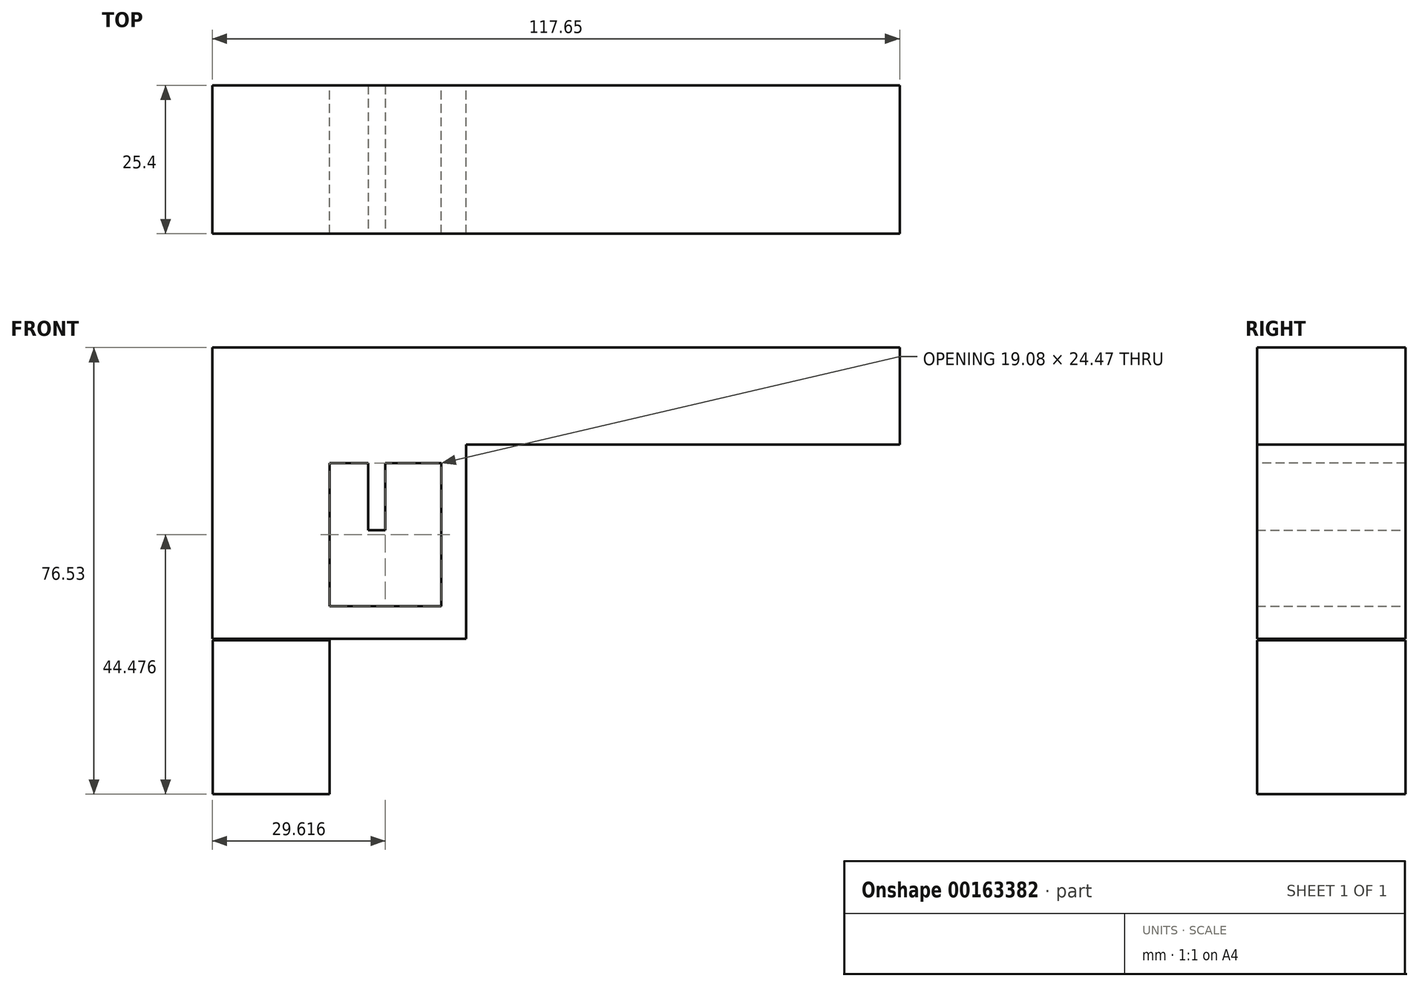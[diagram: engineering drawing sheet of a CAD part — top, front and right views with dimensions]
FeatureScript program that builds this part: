
annotation { "Feature Type Name" : "Feature", "Feature Type Description" : "" }
export const myFeature = defineFeature(function(context is Context, id is Id, definition is map)
    precondition{}
    {
        {
            var Q0;
            Q0=qCreatedBy(makeId("Front.planeOp"),FACE);
            var sketch = newSketch(context, id + "F0", { "sketchPlane" : qUnion([Q0])});
            skLineSegment(sketch, "E0.bottom", {"start": v(-43.44, 19.82) * mm, "end": v(75.73, 19.82) * mm});
            skLineSegment(sketch, "E0.top", {"start": v(-43.44, -30.1) * mm, "end": v(75.73, -30.1) * mm});
            skLineSegment(sketch, "E0.left", {"start": v(-43.44, 19.82) * mm, "end": v(-43.44, -30.1) * mm});
            skLineSegment(sketch, "E0.right", {"start": v(75.73, 19.82) * mm, "end": v(75.73, -30.1) * mm});
            skLineSegment(sketch, "E1.bottom", {"start": v(-35.12, -49.18) * mm, "end": v(-35.85, -49.18) * mm});
            skLineSegment(sketch, "E1.top", {"start": v(-35.12, -48.94) * mm, "end": v(-35.85, -48.94) * mm});
            skLineSegment(sketch, "E1.left", {"start": v(-35.12, -49.18) * mm, "end": v(-35.12, -48.94) * mm});
            skLineSegment(sketch, "E1.right", {"start": v(-35.85, -49.18) * mm, "end": v(-35.85, -48.94) * mm});
            skSolve(sketch);
        }
        {
            var Q0;
            Q0=qCreatedBy(makeId("Front.planeOp"),FACE);
            var sketch = newSketch(context, id + "F1", { "sketchPlane" : qUnion([Q0])});
            skLineSegment(sketch, "E2.bottom", {"start": v(0, -30.1) * mm, "end": v(75.49, -30.1) * mm});
            skLineSegment(sketch, "E2.top", {"start": v(0, 3.18) * mm, "end": v(75.49, 3.18) * mm});
            skLineSegment(sketch, "E2.left", {"start": v(0, -30.1) * mm, "end": v(0, 3.18) * mm});
            skLineSegment(sketch, "E2.right", {"start": v(75.49, -30.1) * mm, "end": v(75.49, 3.18) * mm});
            skSolve(sketch);
        }
        {
            var Q0;
            Q0 = qSketchRegion(id + "F0", true);
            extrude(context, id + "F2", {"entities" : qUnion([Q0]), "depth" : 25.4 * mm});
        }
        {
            var Q0;
            Q0 = qSketchRegion(id + "F1", true);
            extrude(context, id + "F3", {"entities" : qUnion([Q0]), "operationType" : NewBodyOperationType.REMOVE, "depth" : 25.65 * mm});
        }
        {
            var Q0;
            Q0=makeQuery(id+"F2.opExtrude","SWEPT_FACE",FACE,{"disambiguationData":[OSD([sQuery(id+"F0.wireOp",EDGE,"E0.right")])]});
            extrude(context, id + "F4", {"entities" : qUnion([Q0]), "operationType" : NewBodyOperationType.REMOVE, "oppositeDirection" : true, "depth" : 1.52 * mm});
        }
        {
            var Q0;
            Q0=qCreatedBy(makeId("Front.planeOp"),FACE);
            var sketch = newSketch(context, id + "F5", { "sketchPlane" : qUnion([Q0])});
            skLineSegment(sketch, "E3.bottom", {"start": v(-4.28, 0) * mm, "end": v(-23.37, 0) * mm});
            skLineSegment(sketch, "E3.top", {"start": v(-4.28, -24.47) * mm, "end": v(-23.37, -24.47) * mm});
            skLineSegment(sketch, "E3.left", {"start": v(-4.28, 0) * mm, "end": v(-4.28, -24.47) * mm});
            skLineSegment(sketch, "E3.right", {"start": v(-23.37, 0) * mm, "end": v(-23.37, -24.47) * mm});
            skSolve(sketch);
        }
        {
            var Q0;
            Q0 = qSketchRegion(id + "F5", true);
            extrude(context, id + "F6", {"entities" : qUnion([Q0]), "operationType" : NewBodyOperationType.REMOVE, "depth" : 52.32 * mm});
        }
        {
            var Q0;
            Q0=qCreatedBy(makeId("Front.planeOp"),FACE);
            var sketch = newSketch(context, id + "F7", { "sketchPlane" : qUnion([Q0])});
            skLineSegment(sketch, "E4.bottom", {"start": v(-23.37, -30.35) * mm, "end": v(-43.36, -30.35) * mm});
            skLineSegment(sketch, "E4.top", {"start": v(-23.37, -56.71) * mm, "end": v(-43.36, -56.71) * mm});
            skLineSegment(sketch, "E4.left", {"start": v(-23.37, -30.35) * mm, "end": v(-23.37, -56.71) * mm});
            skLineSegment(sketch, "E4.right", {"start": v(-43.36, -30.35) * mm, "end": v(-43.36, -56.71) * mm});
            skLineSegment(sketch, "E5.bottom", {"start": v(-23.37, -39.65) * mm, "end": v(-23.37, -39.65) * mm});
            skLineSegment(sketch, "E5.top", {"start": v(-23.37, -41.98) * mm, "end": v(-23.37, -41.98) * mm});
            skLineSegment(sketch, "E5.left", {"start": v(-23.37, -39.65) * mm, "end": v(-23.37, -41.98) * mm});
            skLineSegment(sketch, "E5.right", {"start": v(-23.37, -39.65) * mm, "end": v(-23.37, -41.98) * mm});
            skSolve(sketch);
        }
        {
            var Q0;
            Q0 = qSketchRegion(id + "F7", true);
            extrude(context, id + "F8", {"entities" : qUnion([Q0]), "operationType" : NewBodyOperationType.ADD, "depth" : 25.4 * mm});
        }
        {
            var Q0;
            Q0=qCreatedBy(makeId("Front.planeOp"),FACE);
            var sketch = newSketch(context, id + "F9", { "sketchPlane" : qUnion([Q0])});
            skLineSegment(sketch, "E6.bottom", {"start": v(-13.85, 2.03) * mm, "end": v(-16.8, 2.03) * mm});
            skLineSegment(sketch, "E6.top", {"start": v(-13.85, -11.48) * mm, "end": v(-16.8, -11.48) * mm});
            skLineSegment(sketch, "E6.left", {"start": v(-13.85, 2.03) * mm, "end": v(-13.85, -11.48) * mm});
            skLineSegment(sketch, "E6.right", {"start": v(-16.8, 2.03) * mm, "end": v(-16.8, -11.48) * mm});
            skSolve(sketch);
        }
        {
            var Q0;
            Q0 = qSketchRegion(id + "F9", true);
            extrude(context, id + "F10", {"entities" : qUnion([Q0]), "operationType" : NewBodyOperationType.ADD, "depth" : 25.4 * mm});
        }
    });
